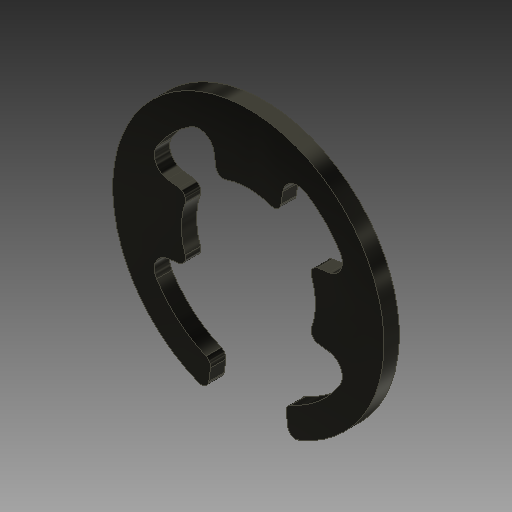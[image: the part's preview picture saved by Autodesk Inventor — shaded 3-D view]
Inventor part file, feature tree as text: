
AUTODESK INVENTOR PART (.ipt)
format: ipt  version: 2018 (Build 220112000, 112)  size: 177,152 bytes
history: native  units: in
note: dims shown in document units (in); Inventor stores cm internally (conversion verified against a paired STEP export)
features: extrude x3, sketch x3, pattern_circular x1, fillet x1, projected_geometry x1
ambient origin geometry x8: Origin, YZ Plane, XZ Plane, XY Plane, X Axis, Y Axis, Z Axis, Center Point
bodies: Solid1 (feature_tree)
feature tree (9):
  extrude  "Extrusion1"  Depth=0.89in
  extrude  "Extrusion2"  Depth=0.05in
  pattern_circular  "Circular Pattern1"  [2 undecoded]
  extrude  "Extrusion3"  Depth=0.025in
  fillet  "Fillet1"  Radius=0.05in
  sketch  "Sketch1"  dims[d0=0.44in d1=0.89in]
  sketch  "Sketch2"  dims[d2=0.05in d3=0.0in d4=0.09in]
  sketch  "Sketch3"  dims[d5=45.0deg d6=0.125in d7=0.3in d8=0.05in d9=0.0in d10=1.5748in d11=360.0deg d13=0.05in d14=0.0in d15=0.05in d16=0.025in]
  projected_geometry  "Projected Loop1"
note: 2 required parameter values undecoded (feature->parameter linkage not recoverable at this tier; creation-order binding heuristic only, values carry confidence <= 0.55)
